# Revit family: QF_NuovAIR_CU-N550T2XL----
name_source: partatom
category: Specialty Equipment
units: mm (PartAtom-declared; Revit-internal decimal feet)

## family parameters
Always vertical = Yes
Cut with Voids When Loaded = No
Part Type = Normal
Room Calculation Point = No
Round Connector Dimension = Use Diameter
Shared = No
Work Plane-Based = No

## types (3) — shared parameters
Accessory = No
CE Approved = Yes
Conn Plug = terminal block
Depth Actual = 1300 mm  [stored 4.26509 ft]
Description = Condensing Unit
Direct Waste Size = 0 mm
Elec Connection Height = 400 mm  [stored 1.31234 ft]
Electric power = 38000000 W
Foodservice Equipment Identifier = Yes
Height Actual = 1780 mm  [stored 5.8399 ft]
Horse Power = 35
Identify Quantity as Lot = No
Item Number = CU-N550T2XL
Keynote = 0
Legs_R = 25 mm  [stored 0.082021 ft]
Length Actual = 3100 mm  [stored 10.1706 ft]
Main switch integrated = No
Manufacturer = NUOVAIR
Mat_Case = QF_Stainless-Brushed
Mat_Clearance = QF_Clearance
Mat_Legs = QF_Stainless-Brushed
Model = CU-N550T2XL
Number of Poles = 3
Phase = 3
Potential Equalisation = Yes
Refrigerant Compressor Remote = No
Refrigerant Type = R452a
Refrigeration Liquid Line Size = 22 mm
Refrigeration Suction Line Size = 54 mm
URL Cutsheet = N550T2XL-en-1.pdf
URL Manufacturer = https://www.nuovair.com
Volt Free Conn = No
Weight = 1133.00 kg
zero-valued in all types: Direct Waste Connection Height

## per-type parameters (varying)
| type | Cycle | FL Amps | Volts |
| CU-N550T2XL_400V 50A | 50 Hz | 76 A | 400 V |
| CU-N550T2XL_440V 60A | 60 Hz | 83 A | 440 V |
| CU-N550T2XL_230V 60A | 60 Hz | 159 A | 230 V |

note: [stored X ft] marks values corroborated as IEEE doubles in the binary element streams (Revit-internal decimal feet)

## geometry (parser evidence)
native form markers: Sweep x6
no freeform markers — native parametric forms only
